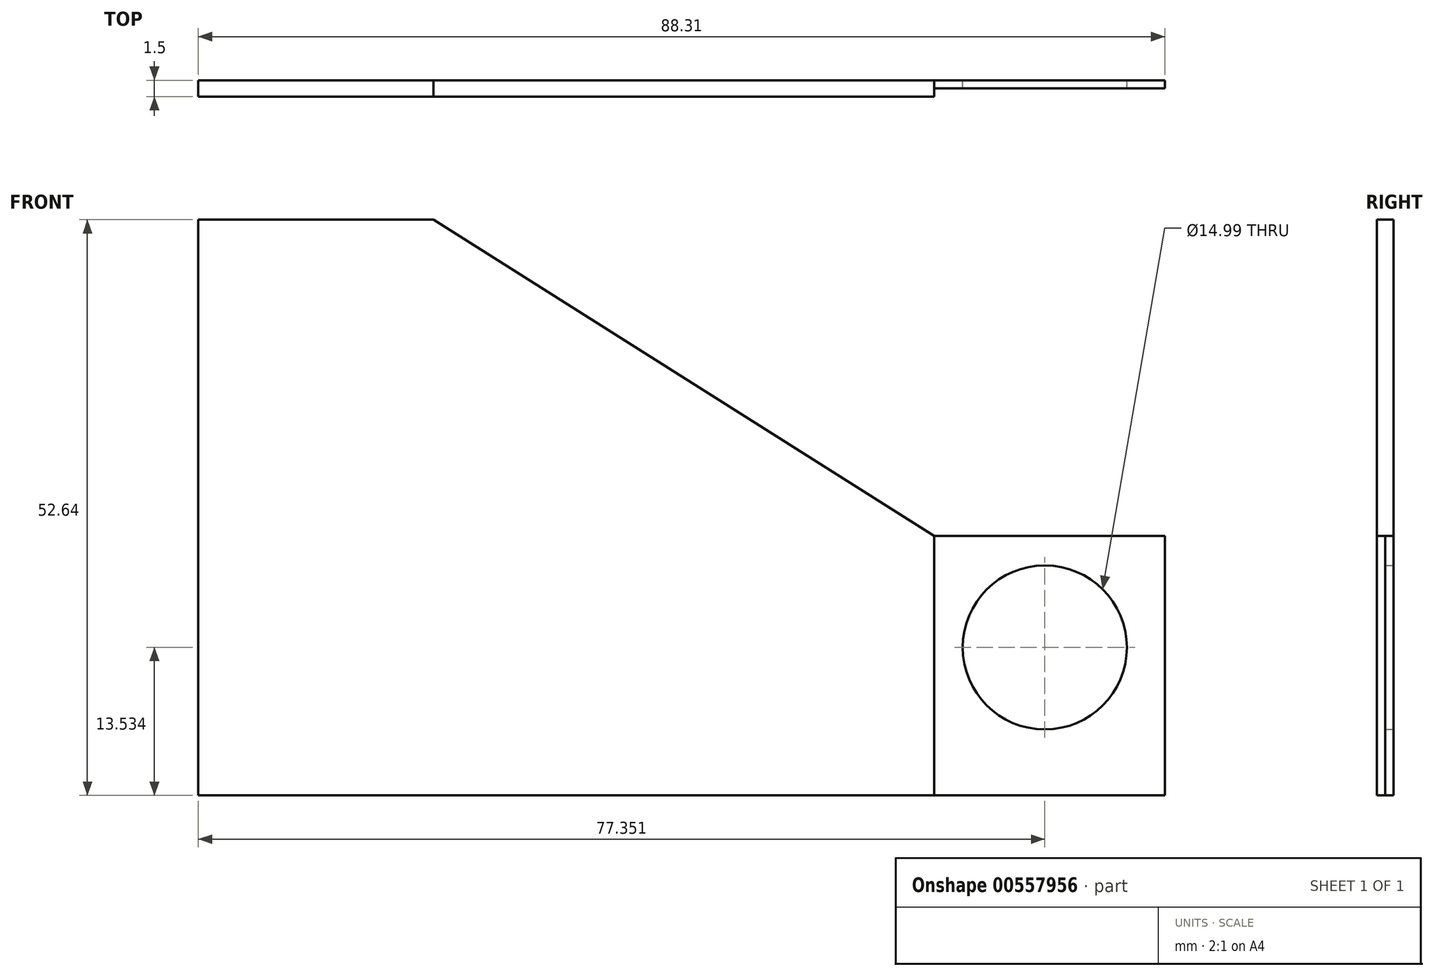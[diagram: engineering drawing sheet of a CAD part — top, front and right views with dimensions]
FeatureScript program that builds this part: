
annotation { "Feature Type Name" : "Feature", "Feature Type Description" : "" }
export const myFeature = defineFeature(function(context is Context, id is Id, definition is map)
    precondition{}
    {
        {
            var Q0;
            Q0=qCreatedBy(makeId("Front.planeOp"),FACE);
            var sketch = newSketch(context, id + "F0", { "sketchPlane" : qUnion([Q0])});
            skLineSegment(sketch, "E0", {"start": v(-45.12, 28.9) * mm, "end": v(-45.12, -23.74) * mm});
            skLineSegment(sketch, "E1", {"start": v(-45.12, -23.74) * mm, "end": v(22.13, -23.74) * mm});
            skLineSegment(sketch, "E2", {"start": v(22.13, -23.74) * mm, "end": v(22.13, 0) * mm});
            skLineSegment(sketch, "E3", {"start": v(-45.12, 28.9) * mm, "end": v(-23.64, 28.9) * mm});
            skLineSegment(sketch, "E4", {"start": v(-23.64, 28.9) * mm, "end": v(22.13, 0) * mm});
            skLineSegment(sketch, "E5", {"start": v(22.13, 0) * mm, "end": v(43.19, 0) * mm});
            skLineSegment(sketch, "E6", {"start": v(43.19, 0) * mm, "end": v(43.19, -23.74) * mm});
            skLineSegment(sketch, "E7", {"start": v(22.13, -23.74) * mm, "end": v(43.19, -23.74) * mm});
            skCircle(sketch, "E8", {"center": v(32.23, -10.2) * mm, "radius": 7.5 * mm});
            skSolve(sketch);
        }
        {
            var Q0;
            Q0=makeQuery(id+"F0.imprint","IMPRINT",FACE,{"disambiguationData":[TD([[makeQuery(id+"F0.imprint","IMPRINT",EDGE,{"derivedFrom":sQuery(id+"F0.wireOp",EDGE,"E0")}),1.0]])]});
            extrude(context, id + "F1", {"entities" : qUnion([Q0]), "depth" : 1.5 * mm, "offsetDistance" : 25 * mm});
        }
        {
            var Q0;
            Q0 = qSketchRegion(id + "F0", true);
            extrude(context, id + "F2", {"entities" : qUnion([Q0]), "operationType" : NewBodyOperationType.ADD, "depth" : .75 * mm, "offsetDistance" : 25 * mm});
        }
    });
